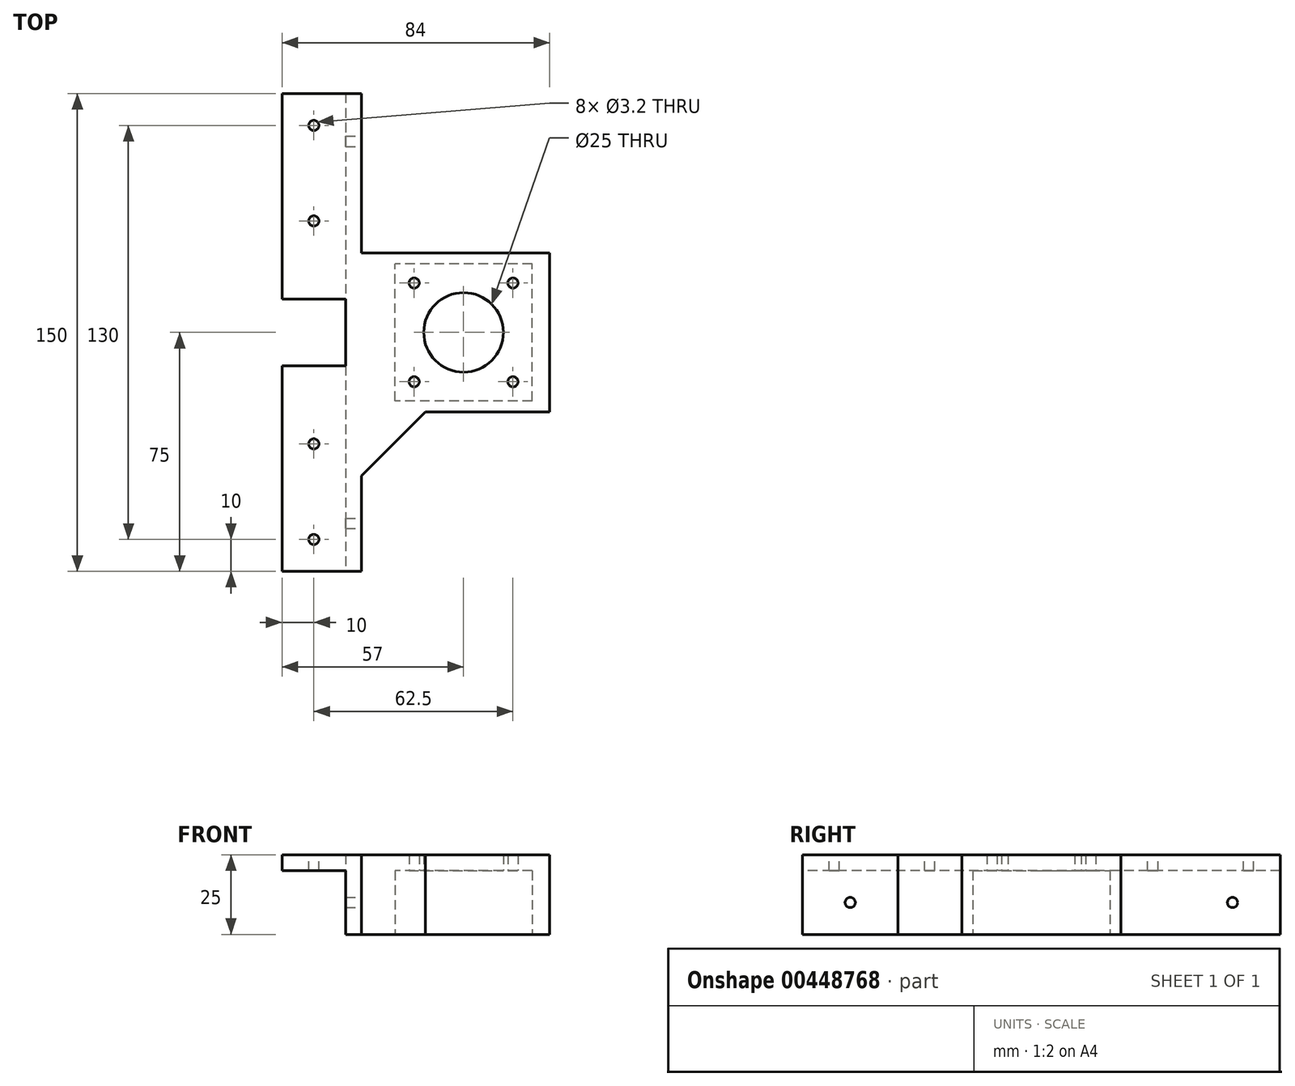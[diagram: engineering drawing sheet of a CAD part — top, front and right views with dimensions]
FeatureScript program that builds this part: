
annotation { "Feature Type Name" : "Feature", "Feature Type Description" : "" }
export const myFeature = defineFeature(function(context is Context, id is Id, definition is map)
    precondition{}
    {
        {
            var Q0;
            Q0=qCreatedBy(makeId("Right.planeOp"),FACE);
            var sketch = newSketch(context, id + "F0", { "sketchPlane" : qUnion([Q0])});
            skLineSegment(sketch, "E0.bottom", {"start": v(0, 0) * mm, "end": v(150, 0) * mm});
            skLineSegment(sketch, "E0.top", {"start": v(0, 25) * mm, "end": v(150, 25) * mm});
            skLineSegment(sketch, "E0.left", {"start": v(0, 0) * mm, "end": v(0, 25) * mm});
            skLineSegment(sketch, "E0.right", {"start": v(150, 0) * mm, "end": v(150, 25) * mm});
            skSolve(sketch);
        }
        {
            var Q0;
            Q0=makeQuery(id+"F0.imprint","IMPRINT",FACE,{"disambiguationData":[TD([[makeQuery(id+"F0.imprint","IMPRINT",EDGE,{"derivedFrom":sQuery(id+"F0.wireOp",EDGE,"E0.bottom")}),1.0]])]});
            extrude(context, id + "F1", {"entities" : qUnion([Q0]), "depth" : 5 * mm});
        }
        {
            var Q0;
            Q0=makeQuery(id+"F1.opExtrude","CAP_FACE",FACE,{"disambiguationData":[OSD([sQuery(id+"F0.wireOp",EDGE,"E0.bottom"),sQuery(id+"F0.wireOp",EDGE,"E0.top"),sQuery(id+"F0.wireOp",EDGE,"E0.left"),sQuery(id+"F0.wireOp",EDGE,"E0.right")])],"isStart":false});
            var sketch = newSketch(context, id + "F2", { "sketchPlane" : qUnion([Q0])});
            skLineSegment(sketch, "E1.bottom", {"start": v(50, 0) * mm, "end": v(100, 0) * mm});
            skLineSegment(sketch, "E1.top", {"start": v(50, 25) * mm, "end": v(100, 25) * mm});
            skLineSegment(sketch, "E1.left", {"start": v(50, 0) * mm, "end": v(50, 25) * mm});
            skLineSegment(sketch, "E1.right", {"start": v(100, 0) * mm, "end": v(100, 25) * mm});
            skPoint(sketch, "E2", {"position": v(75, 25) * mm});
            skSolve(sketch);
        }
        {
            var Q0;
            Q0=makeQuery(id+"F2.imprint","IMPRINT",FACE,{"disambiguationData":[TD([[makeQuery(id+"F2.imprint","IMPRINT",EDGE,{"derivedFrom":sQuery(id+"F2.wireOp",EDGE,"E1.bottom")}),1.0]])]});
            extrude(context, id + "F3", {"entities" : qUnion([Q0]), "operationType" : NewBodyOperationType.ADD, "depth" : 59 * mm});
        }
        {
            var Q0;
            Q0=makeQuery(id+"F3.boolean.opBoolean","MERGE",FACE,{"derivedFrom":[makeQuery(id+"F1.opExtrude","SWEPT_FACE",FACE,{"disambiguationData":[OSD([sQuery(id+"F0.wireOp",EDGE,"E0.bottom")])]}),makeQuery(id+"F3.opExtrude","SWEPT_FACE",FACE,{"disambiguationData":[OSD([sQuery(id+"F2.wireOp",EDGE,"E1.bottom")])]})]});
            var sketch = newSketch(context, id + "F4", { "sketchPlane" : qUnion([Q0])});
            skLineSegment(sketch, "E3.bottom", {"start": v(58.5, -53.5) * mm, "end": v(15.5, -53.5) * mm});
            skLineSegment(sketch, "E3.top", {"start": v(58.5, -96.5) * mm, "end": v(15.5, -96.5) * mm});
            skLineSegment(sketch, "E3.left", {"start": v(58.5, -53.5) * mm, "end": v(58.5, -96.5) * mm});
            skLineSegment(sketch, "E3.right", {"start": v(15.5, -53.5) * mm, "end": v(15.5, -96.5) * mm});
            skSolve(sketch);
        }
        {
            var Q0;
            Q0=makeQuery(id+"F4.imprint","IMPRINT",FACE,{"disambiguationData":[TD([[makeQuery(id+"F4.imprint","IMPRINT",EDGE,{"derivedFrom":sQuery(id+"F4.wireOp",EDGE,"E3.bottom")}),1.0]])]});
            extrude(context, id + "F5", {"entities" : qUnion([Q0]), "operationType" : NewBodyOperationType.REMOVE, "oppositeDirection" : true, "depth" : 20 * mm});
        }
        {
            var Q0;
            Q0=makeQuery(id+"F5.boolean.opBoolean","COPY",FACE,{"derivedFrom":makeQuery(id+"F5.opExtrude","CAP_FACE",FACE,{"disambiguationData":[OSD([sQuery(id+"F4.wireOp",EDGE,"E3.bottom"),sQuery(id+"F4.wireOp",EDGE,"E3.top"),sQuery(id+"F4.wireOp",EDGE,"E3.left"),sQuery(id+"F4.wireOp",EDGE,"E3.right")])],"isStart":false})});
            var sketch = newSketch(context, id + "F6", { "sketchPlane" : qUnion([Q0])});
            skLineSegment(sketch, "E4.bottom", {"start": v(21.5, -59.5) * mm, "end": v(52.5, -59.5) * mm, "construction": true});
            skLineSegment(sketch, "E4.top", {"start": v(21.5, -90.5) * mm, "end": v(52.5, -90.5) * mm, "construction": true});
            skLineSegment(sketch, "E4.left", {"start": v(21.5, -59.5) * mm, "end": v(21.5, -90.5) * mm, "construction": true});
            skLineSegment(sketch, "E4.right", {"start": v(52.5, -59.5) * mm, "end": v(52.5, -90.5) * mm, "construction": true});
            skCircle(sketch, "E5", {"center": v(37, -75) * mm, "radius": 12.5 * mm});
            skPoint(sketch, "E5.centerSnap0", {"position": v(37, -59.5) * mm});
            skPoint(sketch, "E5.centerSnap1", {"position": v(15.5, -75) * mm});
            skSolve(sketch);
        }
        {
            var Q0;
            Q0=sQuery(id+"F6.wireOp",VERTEX,"E4.left.start");
            var Q1;
            Q1=sQuery(id+"F6.wireOp",VERTEX,"E4.right.start");
            var Q2;
            Q2=sQuery(id+"F6.wireOp",VERTEX,"E4.right.end");
            var Q3;
            Q3=sQuery(id+"F6.wireOp",VERTEX,"E4.left.end");
            var Q4;
            Q4=makeQuery(id+"F1.opExtrude","SWEPT_BODY",BODY,{"disambiguationData":[OSD([sQuery(id+"F0.wireOp",EDGE,"E0.bottom"),sQuery(id+"F0.wireOp",EDGE,"E0.top"),sQuery(id+"F0.wireOp",EDGE,"E0.left"),sQuery(id+"F0.wireOp",EDGE,"E0.right")])]});
            hole(context, id + "F7", {"style" : HoleStyle.SIMPLE, "endStyle" : HoleEndStyle.BLIND, "standardTappedOrClearance" : lookupTablePath({ "standard" : "ISO", "size" : "3.2", "type" : "Drilled" }), "standardBlindInLast" : lookupTablePath({ "standard" : "ISO", "size" : "3.2", "type" : "Drilled" }), "holeDiameter" : 3.2 * mm, "holeDepth" : 8 * mm, "locations" : qUnion([Q0, Q1, Q2, Q3]), "scope" : qUnion([Q4])});
        }
        {
            var Q0;
            Q0=makeQuery(id+"F6.imprint","IMPRINT",FACE,{"disambiguationData":[TD([[makeQuery(id+"F6.imprint","IMPRINT",EDGE,{"derivedFrom":sQuery(id+"F6.wireOp",EDGE,"E5")}),1.0]])]});
            extrude(context, id + "F8", {"entities" : qUnion([Q0]), "operationType" : NewBodyOperationType.REMOVE, "endBound" : BoundingType.THROUGH_ALL, "oppositeDirection" : true, "depth" : 25 * mm});
        }
        {
            var Q0;
            {var subQ0=sQuery(id+"F0.wireOp",EDGE,"E0.left");var subQ1=sQuery(id+"F0.wireOp",EDGE,"E0.top");var subQ2=sQuery(id+"F0.wireOp",EDGE,"E0.bottom");Q0=makeQuery(id+"F3.boolean.opBoolean","SPLIT",FACE,{"disambiguationData":[TD([makeQuery(id+"F1.opExtrude","SWEPT_FACE",FACE,{"disambiguationData":[OSD([subQ0])]})])],"derivedFrom":makeQuery(id+"F1.opExtrude","CAP_FACE",FACE,{"disambiguationData":[OSD([subQ2,subQ1,subQ0,sQuery(id+"F0.wireOp",EDGE,"E0.right")])],"isStart":false})});}
            var sketch = newSketch(context, id + "F9", { "sketchPlane" : qUnion([Q0])});
            skLineSegment(sketch, "E6", {"start": v(15, 25) * mm, "end": v(15, 0) * mm, "construction": true});
            skLineSegment(sketch, "E7", {"start": v(0, 10) * mm, "end": v(50, 10) * mm, "construction": true});
            skLineSegment(sketch, "E8", {"start": v(135, 25) * mm, "end": v(135, -5) * mm, "construction": true});
            skLineSegment(sketch, "E9", {"start": v(100, 10) * mm, "end": v(150, 10) * mm, "construction": true});
            skPoint(sketch, "E9.startSnap0", {"position": v(135, 10) * mm});
            skPoint(sketch, "E10", {"position": v(15, 10) * mm});
            skSolve(sketch);
        }
        {
            var Q0;
            Q0=sQuery(id+"F9.wireOp",VERTEX,"E10");
            var Q1;
            Q1=sQuery(id+"F9.wireOp",VERTEX,"E9.startSnap0");
            var Q2;
            Q2=makeQuery(id+"F1.opExtrude","SWEPT_BODY",BODY,{"disambiguationData":[OSD([sQuery(id+"F0.wireOp",EDGE,"E0.bottom"),sQuery(id+"F0.wireOp",EDGE,"E0.top"),sQuery(id+"F0.wireOp",EDGE,"E0.left"),sQuery(id+"F0.wireOp",EDGE,"E0.right")])]});
            hole(context, id + "F10", {"style" : HoleStyle.SIMPLE, "endStyle" : HoleEndStyle.BLIND, "standardTappedOrClearance" : lookupTablePath({ "standard" : "ISO", "size" : "3.2", "type" : "Drilled" }), "standardBlindInLast" : lookupTablePath({ "standard" : "ISO", "size" : "3.2", "type" : "Drilled" }), "holeDiameter" : 3.2 * mm, "holeDepth" : 8 * mm, "locations" : qUnion([Q0, Q1]), "scope" : qUnion([Q2])});
        }
        {
            var Q0;
            Q0=makeQuery(id+"F3.opExtrude","CAP_EDGE",EDGE,{"disambiguationData":[OSD([sQuery(id+"F2.wireOp",EDGE,"E1.left")])],"isStart":true});
            var Q1;
            Q1=makeQuery(id+"F3.opExtrude","CAP_EDGE",EDGE,{"disambiguationData":[OSD([sQuery(id+"F2.wireOp",EDGE,"E1.right")])],"isStart":true});
            chamfer(context, id + "F11", {"entities" : qUnion([Q0, Q1]), "width" : 20 * mm, "tangentPropagation" : true});
        }
        {
            var Q0;
            Q0=makeQuery(id+"F1.opExtrude","CAP_FACE",FACE,{"disambiguationData":[OSD([sQuery(id+"F0.wireOp",EDGE,"E0.bottom"),sQuery(id+"F0.wireOp",EDGE,"E0.top"),sQuery(id+"F0.wireOp",EDGE,"E0.left"),sQuery(id+"F0.wireOp",EDGE,"E0.right")])],"isStart":true});
            var sketch = newSketch(context, id + "F12", { "sketchPlane" : qUnion([Q0])});
            skLineSegment(sketch, "E11.bottom", {"start": v(-150, 25) * mm, "end": v(0, 25) * mm});
            skLineSegment(sketch, "E11.top", {"start": v(-150, 20) * mm, "end": v(0, 20) * mm});
            skLineSegment(sketch, "E11.left", {"start": v(-150, 25) * mm, "end": v(-150, 20) * mm});
            skLineSegment(sketch, "E11.right", {"start": v(0, 25) * mm, "end": v(0, 20) * mm});
            skSolve(sketch);
        }
        {
            var Q0;
            Q0=qSketchRegion(id+"F12",true);
            extrude(context, id + "F13", {"entities" : qUnion([Q0]), "operationType" : NewBodyOperationType.ADD, "depth" : 20 * mm});
        }
        {
            var Q0;
            Q0=makeQuery(id+"F13.opExtrude","CAP_FACE",FACE,{"disambiguationData":[OSD([sQuery(id+"F12.wireOp",EDGE,"E11.bottom"),sQuery(id+"F12.wireOp",EDGE,"E11.top"),sQuery(id+"F12.wireOp",EDGE,"E11.left"),sQuery(id+"F12.wireOp",EDGE,"E11.right")])],"isStart":false});
            var sketch = newSketch(context, id + "F14", { "sketchPlane" : qUnion([Q0])});
            skLineSegment(sketch, "E12.bottom", {"start": v(-85.5, 25) * mm, "end": v(-64.5, 25) * mm});
            skLineSegment(sketch, "E12.top", {"start": v(-85.5, 20) * mm, "end": v(-64.5, 20) * mm});
            skLineSegment(sketch, "E12.left", {"start": v(-85.5, 25) * mm, "end": v(-85.5, 20) * mm});
            skLineSegment(sketch, "E12.right", {"start": v(-64.5, 25) * mm, "end": v(-64.5, 20) * mm});
            skSolve(sketch);
        }
        {
            var Q0;
            Q0=makeQuery(id+"F14.imprint","IMPRINT",FACE,{"disambiguationData":[TD([[makeQuery(id+"F14.imprint","IMPRINT",EDGE,{"derivedFrom":sQuery(id+"F14.wireOp",EDGE,"E12.bottom")}),1.0]])]});
            var Q1;
            Q1=makeQuery(id+"F1.opExtrude","CAP_FACE",FACE,{"disambiguationData":[OSD([sQuery(id+"F0.wireOp",EDGE,"E0.bottom"),sQuery(id+"F0.wireOp",EDGE,"E0.top"),sQuery(id+"F0.wireOp",EDGE,"E0.left"),sQuery(id+"F0.wireOp",EDGE,"E0.right")])],"isStart":true});
            extrude(context, id + "F15", {"entities" : qUnion([Q0]), "operationType" : NewBodyOperationType.REMOVE, "endBound" : BoundingType.UP_TO_SURFACE, "oppositeDirection" : true, "endBoundEntityFace" : qUnion([Q1]), "depth" : 20 * mm});
        }
        {
            var Q0;
            Q0=makeQuery(id+"F13.boolean.opBoolean","MERGE",FACE,{"derivedFrom":[makeQuery(id+"F3.boolean.opBoolean","MERGE",FACE,{"derivedFrom":[makeQuery(id+"F1.opExtrude","SWEPT_FACE",FACE,{"disambiguationData":[OSD([sQuery(id+"F0.wireOp",EDGE,"E0.top")])]}),makeQuery(id+"F3.opExtrude","SWEPT_FACE",FACE,{"disambiguationData":[OSD([sQuery(id+"F2.wireOp",EDGE,"E1.top")])]})]}),makeQuery(id+"F13.opExtrude","SWEPT_FACE",FACE,{"disambiguationData":[OSD([sQuery(id+"F12.wireOp",EDGE,"E11.bottom")])]})]});
            var sketch = newSketch(context, id + "F16", { "sketchPlane" : qUnion([Q0])});
            skLineSegment(sketch, "E13", {"start": v(-10, 0) * mm, "end": v(-10, 150) * mm, "construction": true});
            skPoint(sketch, "E14", {"position": v(-10, 10) * mm});
            skPoint(sketch, "E15", {"position": v(-10, 40) * mm});
            skPoint(sketch, "E16", {"position": v(-10, 110) * mm});
            skPoint(sketch, "E17", {"position": v(-10, 140) * mm});
            skSolve(sketch);
        }
        {
            var Q0;
            Q0=sQuery(id+"F16.wireOp",VERTEX,"E14");
            var Q1;
            Q1=sQuery(id+"F16.wireOp",VERTEX,"E15");
            var Q2;
            Q2=sQuery(id+"F16.wireOp",VERTEX,"E16");
            var Q3;
            Q3=sQuery(id+"F16.wireOp",VERTEX,"E17");
            var Q4;
            Q4=makeQuery(id+"F1.opExtrude","SWEPT_BODY",BODY,{"disambiguationData":[OSD([sQuery(id+"F0.wireOp",EDGE,"E0.bottom"),sQuery(id+"F0.wireOp",EDGE,"E0.top"),sQuery(id+"F0.wireOp",EDGE,"E0.left"),sQuery(id+"F0.wireOp",EDGE,"E0.right")])]});
            hole(context, id + "F17", {"style" : HoleStyle.SIMPLE, "endStyle" : HoleEndStyle.BLIND, "standardTappedOrClearance" : lookupTablePath({ "standard" : "ISO", "size" : "3.2", "type" : "Drilled" }), "standardBlindInLast" : lookupTablePath({ "standard" : "ISO", "size" : "3.2", "type" : "Drilled" }), "holeDiameter" : 3.2 * mm, "holeDepth" : 8 * mm, "locations" : qUnion([Q0, Q1, Q2, Q3]), "scope" : qUnion([Q4])});
        }
    });
